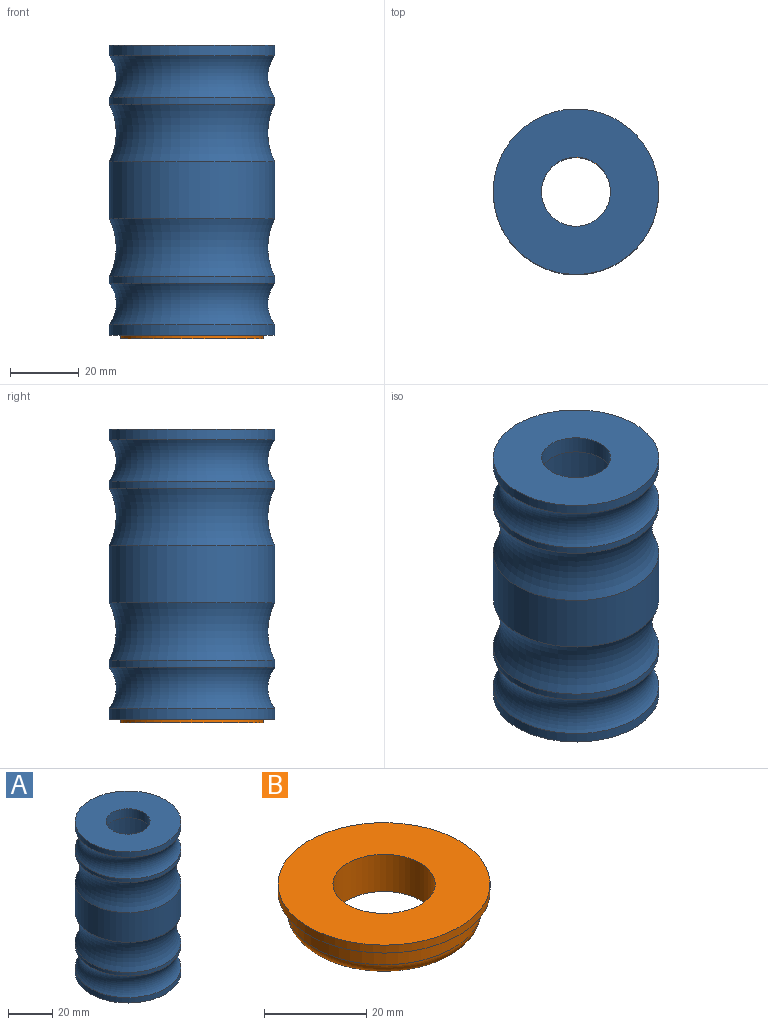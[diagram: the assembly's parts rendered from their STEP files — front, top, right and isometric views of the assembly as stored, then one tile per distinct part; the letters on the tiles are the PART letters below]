
ASSEMBLY  parts=2 mates=1
PART A: 16 faces, bbox 59.2x59.2x84 mm
  f0: cylinder r=20mm len=77mm, axis (0,0,1), area 9676.1mm2, adj f13,f15
  f1: torus R=32mm, axis (0,0,1), area 1833.7mm2, adj f2,f11
  f2: cylinder r=24mm len=48mm, axis (0,0,1), area 301.6mm2, adj f1,f3
  f3: torus R=40.5mm, axis (0,0,1), area 2473.4mm2, adj f2,f4
  f4: cylinder r=24mm len=48mm, axis (0,0,1), area 2493.2mm2, adj f3,f5
  f5: torus R=40.5mm, axis (0,0,1), area 2473.4mm2, adj f4,f6
  f6: cylinder r=24mm len=48mm, axis (0,0,1), area 301.6mm2, adj f5,f7
  f7: torus R=32mm, axis (0,0,1), area 1833.7mm2, adj f6,f8
  f8: cylinder r=24mm len=48mm, axis (0,0,1), area 452.4mm2, adj f7,f9
  f9: plane 48x48mm, normal (0,0,-1), area 424.1mm2, adj f8,f14
  f10: plane 48x48mm, normal (0,0,1), area 1495.4mm2, adj f11,f12
  f11: cylinder r=24mm len=48mm, axis (0,0,1), area 452.4mm2, adj f1,f10
  f12: cylinder r=10mm len=20mm, axis (0,0,1), area 314.2mm2, adj f10,f13
  f13: plane 40x40mm, normal (0,0,-1), area 942.5mm2, adj f0,f12
  f14: cylinder r=21mm len=42mm, axis (0,0,-1), area 263.9mm2, adj f9,f15
  f15: plane 42x42mm, normal (0,0,-1), area 128.8mm2, adj f0,f14
PART B: 7 faces, bbox 41.5x41.5x8.9 mm
  f0: cylinder r=20.75mm len=41.5mm, axis (0,0,-1), area 247.7mm2, adj f2,f3
  f1: cylinder r=10mm len=20mm, axis (0,0,-1), area 559.2mm2, adj f2,f5
  f2: plane 41.5x41.5mm, normal (0,0,1), area 1038.5mm2, adj f0,f1
  f3: plane 41.5x41.5mm, normal (0,0,-1), area 212.6mm2, adj f0,f4
  f4: cylinder r=19.05mm len=38.1mm, axis (0,0,1), area 478.8mm2, adj f3,f6
  f5: plane 32.1x32.1mm, normal (0,0,-1), area 495.1mm2, adj f1,f6
  f6: torus R=16.05mm, axis (0,0,1), area 531.8mm2, adj f4,f5
PLACE A t=(-8.45,68.31,-6.29)mm
PLACE B rot(axis=(1,0,0),180deg) t=(-8.45,68.31,-47.39)mm
MATE cylindrical B.f4 <-> A.f14  axis (0,0,-1) through (-8.45,68.31,-45.39)mm
